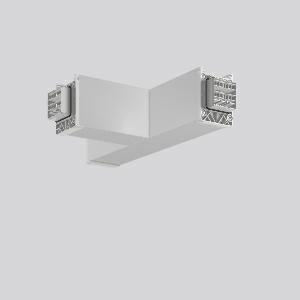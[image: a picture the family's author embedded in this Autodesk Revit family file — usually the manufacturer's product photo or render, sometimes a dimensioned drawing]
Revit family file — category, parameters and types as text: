
# Revit family: linedo_t-verbindung_982774_000_2_908e
name_source: partatom
category: Lighting Fixtures
units: mm (PartAtom-declared; Revit-internal decimal feet)

## family parameters
Cut with Voids When Loaded = No
Host = Face
Light Source = No
Part Type = Normal
Room Calculation Point = No
Round Connector Dimension = Use Diameter
Shared = No

## types (1)
- LINEDO T-Verbindung
    Apparent Load = 0 VA
    Default Elevation = 1800 mm
    Description = Series: LINEDO
T-connector, 14-pole, connection plug / socket - plug. Housing: extruded aluminium profile, anodised. Cover made of plastic, surface like housing. LINEDO plug system, plastic, light grey. Easy connection for rigid or flexible wires. 5 membrane cable entries (2 x M20 and 3 x M25). Suitable for power supply in 7-pole version. Ready prewired. Colour-coded individual cables enable easy electromechanical separation.
Colour: anodised aluminium
Length: 330 mm
Width: 204 mm
Height: 76 mm
Weight: 1070 g
    Height = 76 mm
    Lamp = 0 x
    Length = 331 mm
    Luminous efficacy = 0 lm/W
    Manufacturer = RZB
    ModVariant = No
    Model = 982774.000.2
    Mounting Place = Ceiling
    Mounting Type = Surface mounted
    Number of Poles = 1
    OnlyDefault = Yes
    Power Factor = 1
    Product Name = LINEDO T-Verbindung
    Product group = Surface mounted continuous line luminaire system
    ProductGroupID = 310
    Protection Class = Protection class I
    Protection Degree = Degree of protection
    RLX_Detail_Level = 1
    RLX_Emergency_Light_Flux = 0 lm
    RLX_Emergency_Type = 0
    RLX_Emergency_Type_DB = No
    RlxData = <blob elided: 18209 chars, md5=4c19317c>
    Standby Power = 0 W
    System Light Flux = 0 lm
    System Power = 0 W
    Type Comments = Product without accessories
    Type Image = 982774.000.2.jpg
    URL = http://relux.com
    VarID = ---
    Voltage = 0 V
    Weight = 0.00 kg
    Width = 204 mm

## geometry (parser evidence)
native form markers: Blend x4, Sweep x12
no freeform markers — native parametric forms only
